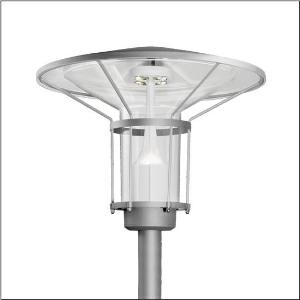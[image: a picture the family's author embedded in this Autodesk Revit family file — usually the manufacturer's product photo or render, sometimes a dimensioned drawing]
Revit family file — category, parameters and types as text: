
# Revit family: laterne_classic_iq___st1_2a_5xa5245af14hp_f3d4
name_source: partatom
category: Lighting Fixtures
units: mm (PartAtom-declared; Revit-internal decimal feet)

## family parameters
Cut with Voids When Loaded = No
Host = Face
Light Source = No
Part Type = Normal
Room Calculation Point = No
Round Connector Dimension = Use Diameter
Shared = No

## types (1)
- --- (1 x LED, 3510 lm, 33.6 W, 2200K)
    Apparent Load = 34 VA
    CIE Flux Codes = 22 60 93 98 100
    Color Rendering = 70
    Color Temperature = 2200K
    Default Elevation = 1800 mm
    Description = Lantern Classic iQ, mast luminaire, Module 540 iQ-SR, primary light control with 3 zone facetted reflector, of plastic, silver coated, highly specular, structured, primary optical cover: cover, of PMMA, transparent, light distribution: ST1.2a, light emission: direct distribution, primary light characteristic: asymmetric, installation type: post-top, LED, High Power LED, rated luminous flux: 3.510lm, luminous efficacy: 105lm/W, light colour: 722, colour temperature: 2200K, control gear: ECG iQ, control: pre-setting: logarithmic dimming characteristic, Street-Remote, Auto-Match, Temp-Guard, Lumen-Switch, Night-Set, Smart-Wire, Light-Fading, Desk-Remote (wireless, voltage-free reading and setting of iQ features in the workshop via application-optimized NFC function/RFID function), optimised constant luminous flux control (CLO 2.0), with terminal, 6-pole, max. 2.5mm², mains connection: 230..240V, AC, 50/60Hz, start of lifetime: 34W, end of service life: 36W, reduction: 15W, luminaire housing, upper part, of glass-fibre reinforced polyester, coated, Siteco® metallic grey (DB 702S), diameter: 750mm, height: 596mm, spigot size: d x l = 76 x 70mm (post-top) | with reducer (optional accessory) 60 x 70mm, post-top mast mounting element, of diecast aluminium, coated, Siteco® metallic grey (DB 702S), Module 540 iQ-SR, traffic white (RAL 9016), equipment: Power, protection rating (complete): IP65, insulation class (complete): insulation class II (safety insulation), certification: CE, ENEC, VDE, packaging unit: 1 piece

Light Distribution: ST1.2a
    Height = 596 mm
    Lamp = 1 x LED
    Lamp Light Flux = 3510 lm
    Lamp Power = 33.6 W
    Lamp count = 1
    Length = 750 mm
    Luminous efficacy = 104 lm/W
    Manufacturer = Siteco
    ModVariant = No
    Model = 5XA5245AF14HP
    Number of Poles = 1
    OnlyDefault = Yes
    Power Factor = 1
    Product Name = Laterne Classic iQ | ST1.2a
    Product group = mast luminaire | pylon top
    ProductGroupID = 6100
    Protection Class = Protection class II
    Protection Degree = IP 65
    RLX_Detail_Level = 1
    RLX_Emergency_Light_Flux = 0 lm
    RLX_Emergency_Type = 0
    RLX_Emergency_Type_DB = No
    RlxData = <blob elided: 64929 chars, md5=b28b4ae4>
    Socket = socket
    Standby Power = 0 W
    System Light Flux = 3510 lm
    System Power = 34 W
    Type Comments = factory setting: luminous flux: 100 % | dim-lin: 254 | 695 mA
    Type Image = l_1006052.jpg
    URL = http://relux.com
    VarID = @adj_166001
    Voltage = 0 V
    Weight = 0.00 kg
    Width = 0 mm  [stored 0 ft]

note: [stored X ft] marks values corroborated as IEEE doubles in the binary element streams (Revit-internal decimal feet)

## geometry (parser evidence)
native form markers: Blend x4, Sweep x11
no freeform markers — native parametric forms only
